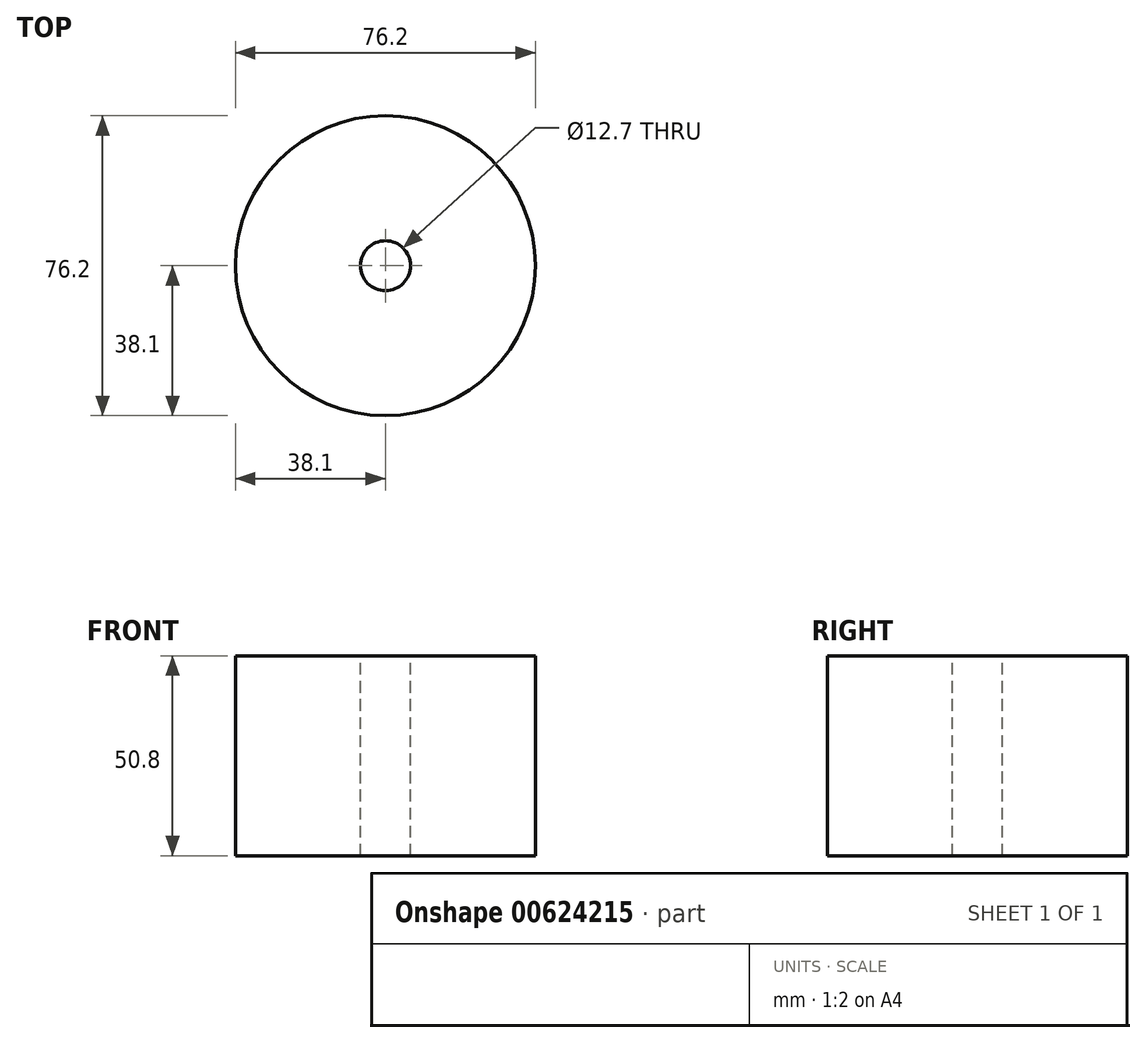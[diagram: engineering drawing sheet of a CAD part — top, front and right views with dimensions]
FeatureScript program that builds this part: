
annotation { "Feature Type Name" : "Feature", "Feature Type Description" : "" }
export const myFeature = defineFeature(function(context is Context, id is Id, definition is map)
    precondition{}
    {
        {
            var Q0;
            Q0=qCreatedBy(makeId("Top.planeOp"),FACE);
            var sketch = newSketch(context, id + "F0", { "sketchPlane" : qUnion([Q0])});
            skCircle(sketch, "E0", {"center": v(0, 0) * mm, "radius": 38.1 * mm});
            skSolve(sketch);
        }
        {
            var Q0;
            Q0=makeQuery(id+"F0.imprint","IMPRINT",FACE,{"disambiguationData":[TD([[makeQuery(id+"F0.imprint","IMPRINT",EDGE,{"derivedFrom":sQuery(id+"F0.wireOp",EDGE,"E0")}),1.0]])]});
            extrude(context, id + "F1", {"entities" : qUnion([Q0]), "depth" : 50.8 * mm, "offsetDistance" : 25.4 * mm});
        }
        {
            var Q0;
            Q0=makeQuery(id+"F1.opExtrude","CAP_FACE",FACE,{"disambiguationData":[OSD([sQuery(id+"F0.wireOp",EDGE,"E0")])],"isStart":false});
            var sketch = newSketch(context, id + "F2", { "sketchPlane" : qUnion([Q0])});
            skCircle(sketch, "E1", {"center": v(0, 0) * mm, "radius": 6.35 * mm});
            skSolve(sketch);
        }
        {
            var Q0;
            Q0=makeQuery(id+"F2.imprint","IMPRINT",FACE,{"disambiguationData":[TD([[makeQuery(id+"F2.imprint","IMPRINT",EDGE,{"derivedFrom":sQuery(id+"F2.wireOp",EDGE,"E1")}),1.0]])]});
            var Q1;
            Q1=sQuery(id+"F2.wireOp",EDGE,"E1");
            extrude(context, id + "F3", {"entities" : qUnion([Q0]), "operationType" : NewBodyOperationType.REMOVE, "surfaceEntities" : qUnion([Q1]), "endBound" : BoundingType.UP_TO_NEXT, "oppositeDirection" : true, "depth" : 25.4 * mm, "offsetDistance" : 25.4 * mm});
        }
    });
